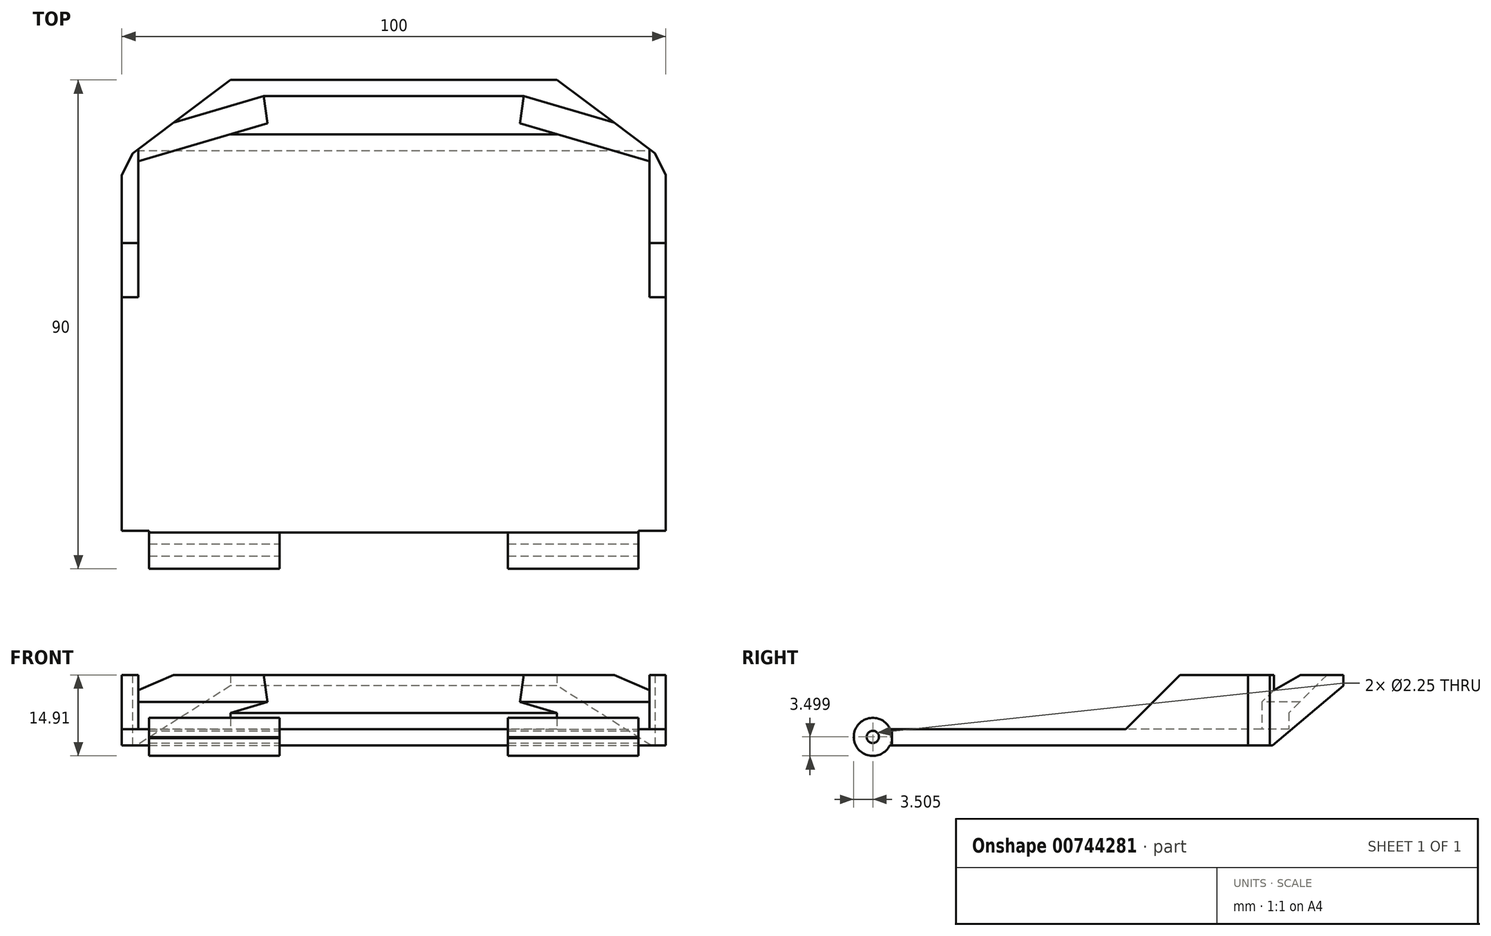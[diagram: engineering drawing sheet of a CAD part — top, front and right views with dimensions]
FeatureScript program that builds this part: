
annotation { "Feature Type Name" : "Feature", "Feature Type Description" : "" }
export const myFeature = defineFeature(function(context is Context, id is Id, definition is map)
    precondition{}
    {
        {
            var Q0;
            Q0=qCreatedBy(makeId("Top.planeOp"),FACE);
            var sketch = newSketch(context, id + "F0", { "sketchPlane" : qUnion([Q0])});
            skLineSegment(sketch, "E0", {"start": v(-30, 54.07) * mm, "end": v(30, 54.07) * mm});
            skLineSegment(sketch, "E1", {"start": v(30, 54.07) * mm, "end": v(50, 39.07) * mm});
            skLineSegment(sketch, "E2", {"start": v(50, 39.07) * mm, "end": v(50, -28.93) * mm});
            skLineSegment(sketch, "E3", {"start": v(45, -35.93) * mm, "end": v(-45, -35.93) * mm});
            skLineSegment(sketch, "E4", {"start": v(-50, -28.93) * mm, "end": v(-50, 39.07) * mm});
            skLineSegment(sketch, "E5", {"start": v(-50, 39.07) * mm, "end": v(-30, 54.07) * mm});
            skLineSegment(sketch, "E6", {"start": v(-45, -35.93) * mm, "end": v(-45, -28.93) * mm});
            skLineSegment(sketch, "E7", {"start": v(-45, -28.93) * mm, "end": v(-50, -28.93) * mm});
            skLineSegment(sketch, "E8.MirrorCS", {"start": v(45, -35.93) * mm, "end": v(45, -28.93) * mm});
            skLineSegment(sketch, "E9.MirrorCS", {"start": v(45, -28.93) * mm, "end": v(50, -28.93) * mm});
            skPoint(sketch, "E10.orphan", {"position": v(-50, -35.93) * mm});
            skSolve(sketch);
        }
        {
            var Q0;
            Q0=makeQuery(id+"F0.imprint","IMPRINT",FACE,{"disambiguationData":[TD([[makeQuery(id+"F0.imprint","IMPRINT",EDGE,{"derivedFrom":sQuery(id+"F0.wireOp",EDGE,"E0")}),-1.0]])]});
            extrude(context, id + "F1", {"entities" : qUnion([Q0]), "depth" : 3 * mm, "offsetDistance" : 25 * mm});
        }
        {
            var Q0;
            Q0=makeQuery(id+"F1.opExtrude","CAP_EDGE",EDGE,{"disambiguationData":[OSD([sQuery(id+"F0.wireOp",EDGE,"E3")])],"isStart":false});
            var Q1;
            Q1=makeQuery(id+"F1.opExtrude","CAP_EDGE",EDGE,{"disambiguationData":[OSD([sQuery(id+"F0.wireOp",EDGE,"E3")])],"isStart":true});
            fillet(context, id + "F2", {"entities" : qUnion([Q0, Q1]), "radius" : 1.5 * mm, "tangentPropagation" : true, "allowEdgeOverflow" : false});
        }
        {
            var Q0;
            Q0=makeQuery(id+"F1.opExtrude","CAP_FACE",FACE,{"disambiguationData":[OSD([sQuery(id+"F0.wireOp",EDGE,"E0"),sQuery(id+"F0.wireOp",EDGE,"E1"),sQuery(id+"F0.wireOp",EDGE,"E2"),sQuery(id+"F0.wireOp",EDGE,"E3"),sQuery(id+"F0.wireOp",EDGE,"E4"),sQuery(id+"F0.wireOp",EDGE,"E5")])],"isStart":false});
            var sketch = newSketch(context, id + "F3", { "sketchPlane" : qUnion([Q0])});
            skLineSegment(sketch, "E11.top", {"start": v(50, 14.07) * mm, "end": v(47, 14.07) * mm});
            skLineSegment(sketch, "E11.left", {"start": v(50, 39.07) * mm, "end": v(50, 14.07) * mm});
            skLineSegment(sketch, "E11.right", {"start": v(47, 39.07) * mm, "end": v(47, 14.07) * mm});
            skLineSegment(sketch, "E12", {"start": v(50, 39.07) * mm, "end": v(30, 54.07) * mm});
            skLineSegment(sketch, "E13", {"start": v(30, 54.07) * mm, "end": v(0, 54.07) * mm});
            skLineSegment(sketch, "E14", {"start": v(0, 44.07) * mm, "end": v(30, 44.07) * mm});
            skLineSegment(sketch, "E15", {"start": v(30, 44.07) * mm, "end": v(47, 39.07) * mm});
            skLineSegment(sketch, "E16.MirrorCS", {"start": v(-50, 14.07) * mm, "end": v(-47, 14.07) * mm});
            skLineSegment(sketch, "E17.MirrorCS", {"start": v(-50, 39.07) * mm, "end": v(-50, 14.07) * mm});
            skLineSegment(sketch, "E18.MirrorCS", {"start": v(-47, 39.07) * mm, "end": v(-47, 14.07) * mm});
            skLineSegment(sketch, "E19.MirrorCS", {"start": v(-30, 44.07) * mm, "end": v(-47, 39.07) * mm});
            skLineSegment(sketch, "E20.MirrorCS", {"start": v(-50, 39.07) * mm, "end": v(-30, 54.07) * mm});
            skLineSegment(sketch, "E21.MirrorCS", {"start": v(-30, 54.07) * mm, "end": v(0, 54.07) * mm});
            skLineSegment(sketch, "E22.MirrorCS", {"start": v(0, 44.07) * mm, "end": v(-30, 44.07) * mm});
            skSolve(sketch);
        }
        {
            var Q0;
            Q0 = qSketchRegion(id + "F3", true);
            extrude(context, id + "F4", {"entities" : qUnion([Q0]), "operationType" : NewBodyOperationType.ADD, "depth" : 10 * mm, "offsetDistance" : 25 * mm});
        }
        {
            var Q0;
            Q0=makeQuery(id+"F4.opExtrude","CAP_EDGE",EDGE,{"disambiguationData":[OSD([sQuery(id+"F3.wireOp",EDGE,"E11.top")])],"isStart":false});
            var Q1;
            Q1=makeQuery(id+"F4.opExtrude","CAP_EDGE",EDGE,{"disambiguationData":[OSD([sQuery(id+"F3.wireOp",EDGE,"E16.MirrorCS")])],"isStart":false});
            chamfer(context, id + "F5", {"entities" : qUnion([Q0, Q1]), "width" : 10 * mm, "tangentPropagation" : true});
        }
        {
            var Q0;
            Q0=makeQuery(id+"F1.opExtrude","CAP_EDGE",EDGE,{"disambiguationData":[OSD([sQuery(id+"F0.wireOp",EDGE,"E0")])],"isStart":true});
            chamfer(context, id + "F6", {"entities" : qUnion([Q0]), "chamferType" : ChamferType.TWO_OFFSETS, "width1" : 13 * mm, "oppositeDirection" : false, "width2" : 11 * mm, "tangentPropagation" : true});
        }
        {
            var Q0;
            Q0=makeQuery(id+"F4.opExtrude","CAP_EDGE",EDGE,{"disambiguationData":[OSD([sQuery(id+"F3.wireOp",EDGE,"E14"),sQuery(id+"F3.wireOp",EDGE,"E22.MirrorCS")])],"isStart":false});
            chamfer(context, id + "F7", {"entities" : qUnion([Q0]), "width" : 7 * mm, "tangentPropagation" : true});
        }
        {
            var Q0;
            Q0=makeQuery(id+"F4.opExtrude","CAP_EDGE",EDGE,{"disambiguationData":[OSD([sQuery(id+"F3.wireOp",EDGE,"E19.MirrorCS")])],"isStart":false});
            var Q1;
            Q1=makeQuery(id+"F4.opExtrude","CAP_EDGE",EDGE,{"disambiguationData":[OSD([sQuery(id+"F3.wireOp",EDGE,"E15")])],"isStart":false});
            chamfer(context, id + "F8", {"entities" : qUnion([Q0, Q1]), "width" : 5 * mm, "tangentPropagation" : true});
        }
        {
            var Q0;
            Q0=makeQuery(id+"F4.boolean.opBoolean","MERGE",EDGE,{"derivedFrom":[makeQuery(id+"F1.opExtrude","SWEPT_EDGE",EDGE,{"disambiguationData":[OSD([sQuery(id+"F0.wireOp",EDGE,"E4"),sQuery(id+"F0.wireOp",EDGE,"E5")])]}),makeQuery(id+"F4.opExtrude","SWEPT_EDGE",EDGE,{"disambiguationData":[OSD([sQuery(id+"F3.wireOp",EDGE,"E17.MirrorCS"),sQuery(id+"F3.wireOp",EDGE,"E20.MirrorCS")])]})]});
            var Q1;
            Q1=makeQuery(id+"F4.boolean.opBoolean","MERGE",EDGE,{"derivedFrom":[makeQuery(id+"F1.opExtrude","SWEPT_EDGE",EDGE,{"disambiguationData":[OSD([sQuery(id+"F0.wireOp",EDGE,"E1"),sQuery(id+"F0.wireOp",EDGE,"E2")])]}),makeQuery(id+"F4.opExtrude","SWEPT_EDGE",EDGE,{"disambiguationData":[OSD([sQuery(id+"F3.wireOp",EDGE,"E11.left"),sQuery(id+"F3.wireOp",EDGE,"E12")])]})]});
            chamfer(context, id + "F9", {"entities" : qUnion([Q0, Q1]), "width" : 5 * mm, "tangentPropagation" : true});
        }
        {
            var Q0;
            Q0=makeQuery(id+"F4.boolean.opBoolean","MERGE",FACE,{"derivedFrom":[makeQuery(id+"F1.opExtrude","SWEPT_FACE",FACE,{"disambiguationData":[OSD([sQuery(id+"F0.wireOp",EDGE,"E2")])]}),makeQuery(id+"F4.opExtrude","SWEPT_FACE",FACE,{"disambiguationData":[OSD([sQuery(id+"F3.wireOp",EDGE,"E11.left")])]})]});
            cPlane(context, id + "F10", {"entities" : qUnion([Q0]), "cplaneType" : CPlaneType.OFFSET, "offset" : 5 * mm, "oppositeDirection" : true, "width" : 150 * mm, "height" : 150 * mm});
        }
        {
            var Q0;
            Q0=qCreatedBy(id+"F10.planeOp",FACE);
            var sketch = newSketch(context, id + "F11", { "sketchPlane" : qUnion([Q0])});
            skCircle(sketch, "E23", {"center": v(-32.43, 1.59) * mm, "radius": 3.5 * mm});
            skSolve(sketch);
        }
        {
            var Q0;
            Q0 = qSketchRegion(id + "F11", true);
            extrude(context, id + "F12", {"entities" : qUnion([Q0]), "operationType" : NewBodyOperationType.ADD, "oppositeDirection" : true, "depth" : 90 * mm, "offsetDistance" : 25 * mm});
        }
        {
            var Q0;
            {var subQ0=sQuery(id+"F0.wireOp",EDGE,"E3");var subQ1=sQuery(id+"F11.wireOp",EDGE,"E23");Q0=makeQuery(id+"F12.boolean.opBoolean","SPLIT",FACE,{"disambiguationData":[TD([makeQuery(id+"F1.opExtrude","CAP_FACE",FACE,{"disambiguationData":[OSD([sQuery(id+"F0.wireOp",EDGE,"E0"),sQuery(id+"F0.wireOp",EDGE,"E1"),sQuery(id+"F0.wireOp",EDGE,"E2"),subQ0,sQuery(id+"F0.wireOp",EDGE,"E4"),sQuery(id+"F0.wireOp",EDGE,"E5")])],"isStart":false})])],"derivedFrom":makeQuery(id+"F12.opExtrude","CAP_FACE",FACE,{"disambiguationData":[OSD([subQ1])],"isStart":true})});}
            var sketch = newSketch(context, id + "F13", { "sketchPlane" : qUnion([Q0])});
            skCircle(sketch, "E24", {"center": v(-32.43, 1.59) * mm, "radius": 1.13 * mm});
            skSolve(sketch);
        }
        {
            var Q0;
            Q0 = qSketchRegion(id + "F13", true);
            extrude(context, id + "F14", {"entities" : qUnion([Q0]), "operationType" : NewBodyOperationType.REMOVE, "oppositeDirection" : true, "depth" : 90 * mm, "offsetDistance" : 25 * mm});
        }
        {
            var Q0;
            Q0=qCreatedBy(makeId("Top.planeOp"),FACE);
            var sketch = newSketch(context, id + "F15", { "sketchPlane" : qUnion([Q0])});
            skLineSegment(sketch, "E25.bottom", {"start": v(-21, -29.22) * mm, "end": v(21, -29.22) * mm});
            skLineSegment(sketch, "E25.top", {"start": v(-21, -38.48) * mm, "end": v(21, -38.48) * mm});
            skLineSegment(sketch, "E25.left", {"start": v(-21, -29.22) * mm, "end": v(-21, -38.48) * mm});
            skLineSegment(sketch, "E25.right", {"start": v(21, -29.22) * mm, "end": v(21, -38.48) * mm});
            skSolve(sketch);
        }
        {
            var Q0;
            Q0 = qSketchRegion(id + "F15", true);
            extrude(context, id + "F16", {"entities" : qUnion([Q0]), "operationType" : NewBodyOperationType.REMOVE, "depth" : 32.7 * mm, "offsetDistance" : 25 * mm});
        }
        {
            var Q0;
            Q0=makeQuery(id+"F16.boolean.opBoolean","COPY",FACE,{"derivedFrom":makeQuery(id+"F16.opExtrude","CAP_FACE",FACE,{"disambiguationData":[OSD([sQuery(id+"F15.wireOp",EDGE,"E25.bottom"),sQuery(id+"F15.wireOp",EDGE,"E25.top"),sQuery(id+"F15.wireOp",EDGE,"E25.left"),sQuery(id+"F15.wireOp",EDGE,"E25.right")])],"isStart":true})});
            var sketch = newSketch(context, id + "F17", { "sketchPlane" : qUnion([Q0])});
            skLineSegment(sketch, "E26.bottom", {"start": v(-21, -29.3) * mm, "end": v(21, -29.3) * mm});
            skLineSegment(sketch, "E26.top", {"start": v(-21, -35.54) * mm, "end": v(21, -35.54) * mm});
            skLineSegment(sketch, "E26.left", {"start": v(-21, -29.3) * mm, "end": v(-21, -35.54) * mm});
            skLineSegment(sketch, "E26.right", {"start": v(21, -29.3) * mm, "end": v(21, -35.54) * mm});
            skSolve(sketch);
        }
        {
            var Q0;
            Q0 = qSketchRegion(id + "F17", true);
            extrude(context, id + "F18", {"entities" : qUnion([Q0]), "operationType" : NewBodyOperationType.REMOVE, "oppositeDirection" : true, "depth" : 25 * mm, "offsetDistance" : 25 * mm});
        }
    });
